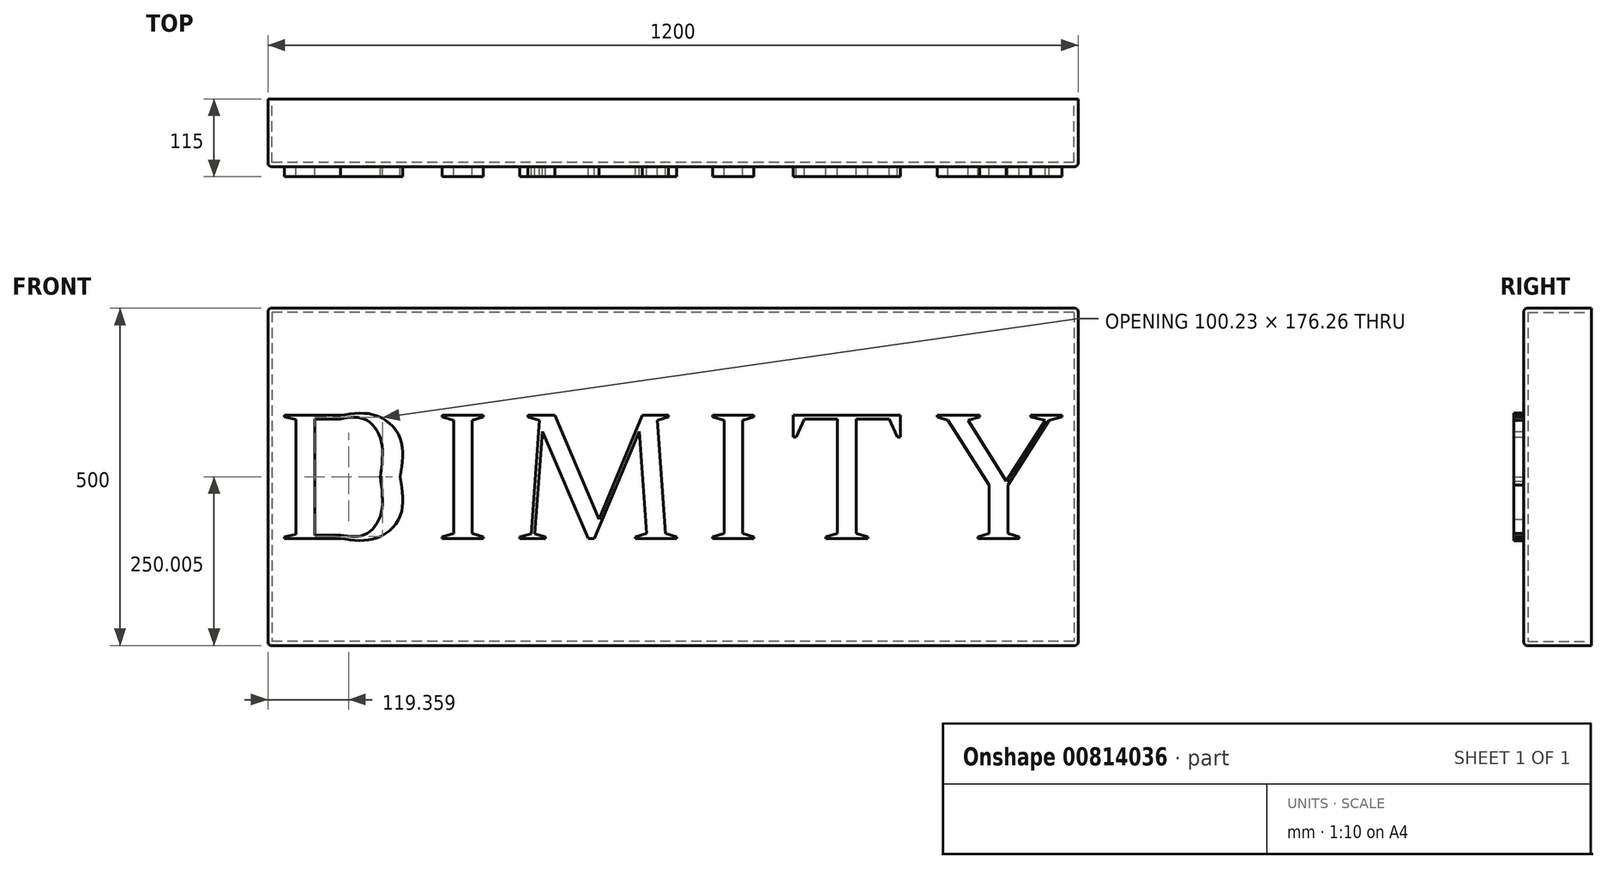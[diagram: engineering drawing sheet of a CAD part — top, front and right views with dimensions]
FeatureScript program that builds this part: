
annotation { "Feature Type Name" : "Feature", "Feature Type Description" : "" }
export const myFeature = defineFeature(function(context is Context, id is Id, definition is map)
    precondition{}
    {
        {
            var Q0;
            Q0=qCreatedBy(makeId("Front.planeOp"),FACE);
            var sketch = newSketch(context, id + "F0", { "sketchPlane" : qUnion([Q0])});
            skLineSegment(sketch, "E0", {"start": v(-575.86, 131.85) * mm, "end": v(-575.86, 129.5) * mm});
            skLineSegment(sketch, "E1", {"start": v(-575.86, 129.5) * mm, "end": v(-558.92, 125.59) * mm});
            skLineSegment(sketch, "E2", {"start": v(-558.92, 125.59) * mm, "end": v(-558.92, -44.41) * mm});
            skLineSegment(sketch, "E3", {"start": v(-558.92, -44.41) * mm, "end": v(-575.86, -48.59) * mm});
            skLineSegment(sketch, "E4", {"start": v(-575.86, -48.59) * mm, "end": v(-575.86, -50.67) * mm});
            skLineSegment(sketch, "E5", {"start": v(-575.86, -50.67) * mm, "end": v(-492.69, -50.67) * mm});
            skFitSpline(sketch, "E6", {"points": [v(-492.69, -50.67) * mm, v(-440.54, -50.67) * mm, v(-404.04, -16.78) * mm, v(-404.04, 40.59) * mm]});
            skFitSpline(sketch, "E7", {"points": [v(-404.04, 40.59) * mm, v(-404.04, 97.43) * mm, v(-440.54, 131.85) * mm, v(-492.69, 131.85) * mm]});
            skLineSegment(sketch, "E8", {"start": v(-492.69, 131.85) * mm, "end": v(-575.86, 131.85) * mm});
            skLineSegment(sketch, "E9", {"start": v(-530.76, 126.63) * mm, "end": v(-492.69, 126.63) * mm});
            skFitSpline(sketch, "E10", {"points": [v(-492.69, 126.63) * mm, v(-458.27, 126.63) * mm, v(-433.5, 97.95) * mm, v(-433.5, 40.33) * mm]});
            skFitSpline(sketch, "E11", {"points": [v(-433.5, 40.33) * mm, v(-433.5, -17.04) * mm, v(-458.27, -45.46) * mm, v(-492.69, -45.46) * mm]});
            skLineSegment(sketch, "E12", {"start": v(-492.69, -45.46) * mm, "end": v(-530.76, -45.46) * mm});
            skLineSegment(sketch, "E13", {"start": v(-530.76, -45.46) * mm, "end": v(-530.76, 126.63) * mm});
            skLineSegment(sketch, "E14", {"start": v(-341.97, 131.85) * mm, "end": v(-341.97, 129.24) * mm});
            skLineSegment(sketch, "E15", {"start": v(-341.97, 129.24) * mm, "end": v(-325.02, 124.28) * mm});
            skLineSegment(sketch, "E16", {"start": v(-325.02, 124.28) * mm, "end": v(-325.02, -43.11) * mm});
            skLineSegment(sketch, "E17", {"start": v(-325.02, -43.11) * mm, "end": v(-341.97, -48.06) * mm});
            skLineSegment(sketch, "E18", {"start": v(-341.97, -48.06) * mm, "end": v(-341.97, -50.67) * mm});
            skLineSegment(sketch, "E19", {"start": v(-341.97, -50.67) * mm, "end": v(-281.21, -50.67) * mm});
            skLineSegment(sketch, "E20", {"start": v(-281.21, -50.67) * mm, "end": v(-281.21, -48.06) * mm});
            skLineSegment(sketch, "E21", {"start": v(-281.21, -48.06) * mm, "end": v(-297.38, -43.11) * mm});
            skLineSegment(sketch, "E22", {"start": v(-297.38, -43.11) * mm, "end": v(-297.38, 124.28) * mm});
            skLineSegment(sketch, "E23", {"start": v(-297.38, 124.28) * mm, "end": v(-281.21, 129.24) * mm});
            skLineSegment(sketch, "E24", {"start": v(-281.21, 129.24) * mm, "end": v(-281.21, 131.85) * mm});
            skLineSegment(sketch, "E25", {"start": v(-281.21, 131.85) * mm, "end": v(-341.97, 131.85) * mm});
            skLineSegment(sketch, "E26", {"start": v(-214.99, 131.85) * mm, "end": v(-214.99, 129.24) * mm});
            skLineSegment(sketch, "E27", {"start": v(-214.99, 129.24) * mm, "end": v(-198.04, 124.28) * mm});
            skLineSegment(sketch, "E28", {"start": v(-198.04, 124.28) * mm, "end": v(-210.3, -43.63) * mm});
            skLineSegment(sketch, "E29", {"start": v(-210.3, -43.63) * mm, "end": v(-227.24, -48.59) * mm});
            skLineSegment(sketch, "E30", {"start": v(-227.24, -48.59) * mm, "end": v(-227.24, -50.67) * mm});
            skLineSegment(sketch, "E31", {"start": v(-227.24, -50.67) * mm, "end": v(-188.91, -50.67) * mm});
            skLineSegment(sketch, "E32", {"start": v(-188.91, -50.67) * mm, "end": v(-188.91, -48.59) * mm});
            skLineSegment(sketch, "E33", {"start": v(-188.91, -48.59) * mm, "end": v(-204.82, -43.63) * mm});
            skLineSegment(sketch, "E34", {"start": v(-204.82, -43.63) * mm, "end": v(-193.6, 108.12) * mm});
            skLineSegment(sketch, "E35", {"start": v(-193.6, 108.12) * mm, "end": v(-125.55, -50.67) * mm});
            skLineSegment(sketch, "E36", {"start": v(-125.55, -50.67) * mm, "end": v(-116.95, -50.67) * mm});
            skLineSegment(sketch, "E37", {"start": v(-116.95, -50.67) * mm, "end": v(-49.94, 107.86) * mm});
            skLineSegment(sketch, "E38", {"start": v(-49.94, 107.86) * mm, "end": v(-38.99, -43.11) * mm});
            skLineSegment(sketch, "E39", {"start": v(-38.99, -43.11) * mm, "end": v(-55.94, -48.06) * mm});
            skLineSegment(sketch, "E40", {"start": v(-55.94, -48.06) * mm, "end": v(-55.94, -50.67) * mm});
            skLineSegment(sketch, "E41", {"start": v(-55.94, -50.67) * mm, "end": v(5.08, -50.67) * mm});
            skLineSegment(sketch, "E42", {"start": v(5.08, -50.67) * mm, "end": v(5.08, -48.06) * mm});
            skLineSegment(sketch, "E43", {"start": v(5.08, -48.06) * mm, "end": v(-11.1, -43.11) * mm});
            skLineSegment(sketch, "E44", {"start": v(-11.1, -43.11) * mm, "end": v(-23.08, 124.28) * mm});
            skLineSegment(sketch, "E45", {"start": v(-23.08, 124.28) * mm, "end": v(-6.92, 129.24) * mm});
            skLineSegment(sketch, "E46", {"start": v(-6.92, 129.24) * mm, "end": v(-6.92, 131.85) * mm});
            skLineSegment(sketch, "E47", {"start": v(-6.92, 131.85) * mm, "end": v(-45.25, 131.85) * mm});
            skLineSegment(sketch, "E48", {"start": v(-45.25, 131.85) * mm, "end": v(-109.9, -21.99) * mm});
            skLineSegment(sketch, "E49", {"start": v(-109.9, -21.99) * mm, "end": v(-175.1, 131.85) * mm});
            skLineSegment(sketch, "E50", {"start": v(-175.1, 131.85) * mm, "end": v(-214.99, 131.85) * mm});
            skLineSegment(sketch, "E51", {"start": v(58.54, 131.85) * mm, "end": v(58.54, 129.24) * mm});
            skLineSegment(sketch, "E52", {"start": v(58.54, 129.24) * mm, "end": v(75.5, 124.28) * mm});
            skLineSegment(sketch, "E53", {"start": v(75.5, 124.28) * mm, "end": v(75.5, -43.11) * mm});
            skLineSegment(sketch, "E54", {"start": v(75.5, -43.11) * mm, "end": v(58.54, -48.06) * mm});
            skLineSegment(sketch, "E55", {"start": v(58.54, -48.06) * mm, "end": v(58.54, -50.67) * mm});
            skLineSegment(sketch, "E56", {"start": v(58.54, -50.67) * mm, "end": v(119.3, -50.67) * mm});
            skLineSegment(sketch, "E57", {"start": v(119.3, -50.67) * mm, "end": v(119.3, -48.06) * mm});
            skLineSegment(sketch, "E58", {"start": v(119.3, -48.06) * mm, "end": v(103.13, -43.11) * mm});
            skLineSegment(sketch, "E59", {"start": v(103.13, -43.11) * mm, "end": v(103.13, 124.28) * mm});
            skLineSegment(sketch, "E60", {"start": v(103.13, 124.28) * mm, "end": v(119.3, 129.24) * mm});
            skLineSegment(sketch, "E61", {"start": v(119.3, 129.24) * mm, "end": v(119.3, 131.85) * mm});
            skLineSegment(sketch, "E62", {"start": v(119.3, 131.85) * mm, "end": v(58.54, 131.85) * mm});
            skLineSegment(sketch, "E63", {"start": v(178.23, 131.85) * mm, "end": v(178.23, 99.77) * mm});
            skLineSegment(sketch, "E64", {"start": v(178.23, 99.77) * mm, "end": v(182.4, 99.77) * mm});
            skLineSegment(sketch, "E65", {"start": v(182.4, 99.77) * mm, "end": v(194.65, 126.63) * mm});
            skLineSegment(sketch, "E66", {"start": v(194.65, 126.63) * mm, "end": v(243.15, 126.63) * mm});
            skLineSegment(sketch, "E67", {"start": v(243.15, 126.63) * mm, "end": v(243.15, -43.11) * mm});
            skLineSegment(sketch, "E68", {"start": v(243.15, -43.11) * mm, "end": v(226.2, -48.06) * mm});
            skLineSegment(sketch, "E69", {"start": v(226.2, -48.06) * mm, "end": v(226.2, -50.67) * mm});
            skLineSegment(sketch, "E70", {"start": v(226.2, -50.67) * mm, "end": v(288.26, -50.67) * mm});
            skLineSegment(sketch, "E71", {"start": v(288.26, -50.67) * mm, "end": v(288.26, -48.06) * mm});
            skLineSegment(sketch, "E72", {"start": v(288.26, -48.06) * mm, "end": v(271.31, -43.11) * mm});
            skLineSegment(sketch, "E73", {"start": v(271.31, -43.11) * mm, "end": v(271.31, 126.63) * mm});
            skLineSegment(sketch, "E74", {"start": v(271.31, 126.63) * mm, "end": v(320.07, 126.63) * mm});
            skLineSegment(sketch, "E75", {"start": v(320.07, 126.63) * mm, "end": v(332.06, 99.77) * mm});
            skLineSegment(sketch, "E76", {"start": v(332.06, 99.77) * mm, "end": v(336.5, 99.77) * mm});
            skLineSegment(sketch, "E77", {"start": v(336.5, 99.77) * mm, "end": v(336.5, 131.85) * mm});
            skLineSegment(sketch, "E78", {"start": v(336.5, 131.85) * mm, "end": v(178.23, 131.85) * mm});
            skLineSegment(sketch, "E79", {"start": v(391.26, 131.85) * mm, "end": v(391.26, 129.24) * mm});
            skLineSegment(sketch, "E80", {"start": v(391.26, 129.24) * mm, "end": v(407.43, 124.28) * mm});
            skLineSegment(sketch, "E81", {"start": v(407.43, 124.28) * mm, "end": v(468.44, 28.6) * mm});
            skLineSegment(sketch, "E82", {"start": v(468.44, 28.6) * mm, "end": v(468.44, -43.11) * mm});
            skLineSegment(sketch, "E83", {"start": v(468.44, -43.11) * mm, "end": v(451.5, -48.06) * mm});
            skLineSegment(sketch, "E84", {"start": v(451.5, -48.06) * mm, "end": v(451.5, -50.67) * mm});
            skLineSegment(sketch, "E85", {"start": v(451.5, -50.67) * mm, "end": v(512.5, -50.67) * mm});
            skLineSegment(sketch, "E86", {"start": v(512.5, -50.67) * mm, "end": v(512.5, -48.06) * mm});
            skLineSegment(sketch, "E87", {"start": v(512.5, -48.06) * mm, "end": v(496.34, -43.11) * mm});
            skLineSegment(sketch, "E88", {"start": v(496.34, -43.11) * mm, "end": v(496.34, 28.6) * mm});
            skLineSegment(sketch, "E89", {"start": v(496.34, 28.6) * mm, "end": v(557.35, 124.28) * mm});
            skLineSegment(sketch, "E90", {"start": v(557.35, 124.28) * mm, "end": v(575.86, 129.24) * mm});
            skLineSegment(sketch, "E91", {"start": v(575.86, 129.24) * mm, "end": v(575.86, 131.85) * mm});
            skLineSegment(sketch, "E92", {"start": v(575.86, 131.85) * mm, "end": v(529.46, 131.85) * mm});
            skLineSegment(sketch, "E93", {"start": v(529.46, 131.85) * mm, "end": v(529.46, 129.24) * mm});
            skLineSegment(sketch, "E94", {"start": v(529.46, 129.24) * mm, "end": v(551.36, 124.28) * mm});
            skLineSegment(sketch, "E95", {"start": v(551.36, 124.28) * mm, "end": v(493.74, 34.33) * mm});
            skLineSegment(sketch, "E96", {"start": v(493.74, 34.33) * mm, "end": v(436.9, 124.28) * mm});
            skLineSegment(sketch, "E97", {"start": v(436.9, 124.28) * mm, "end": v(454.1, 129.24) * mm});
            skLineSegment(sketch, "E98", {"start": v(454.1, 129.24) * mm, "end": v(454.1, 131.85) * mm});
            skLineSegment(sketch, "E99", {"start": v(454.1, 131.85) * mm, "end": v(391.26, 131.85) * mm});
            skSolve(sketch);
        }
        {
            var Q0;
            Q0=qSketchRegion(id+"F0",true);
            extrude(context, id + "F1", {"entities" : qUnion([Q0]), "depth" : 15 * mm, "offsetDistance" : 25 * mm});
        }
        {
            var Q0;
            Q0=qCreatedBy(makeId("Front.planeOp"),FACE);
            var sketch = newSketch(context, id + "F2", { "sketchPlane" : qUnion([Q0])});
            skLineSegment(sketch, "E100.bottom", {"start": v(600, 290.59) * mm, "end": v(-600, 290.59) * mm});
            skLineSegment(sketch, "E100.top", {"start": v(600, -209.41) * mm, "end": v(-600, -209.41) * mm});
            skLineSegment(sketch, "E100.left", {"start": v(600, 290.59) * mm, "end": v(600, -209.41) * mm});
            skLineSegment(sketch, "E100.right", {"start": v(-600, 290.59) * mm, "end": v(-600, -209.41) * mm});
            skLineSegment(sketch, "E101", {"start": v(0, -209.41) * mm, "end": v(-600, -209.41) * mm, "construction": true});
            skLineSegment(sketch, "E102", {"start": v(-600, 265.59) * mm, "end": v(600, 265.59) * mm, "construction": true});
            skLineSegment(sketch, "E103", {"start": v(600, -184.41) * mm, "end": v(-600, -184.41) * mm, "construction": true});
            skLineSegment(sketch, "E104", {"start": v(0, 290.59) * mm, "end": v(0, -209.41) * mm, "construction": true});
            skLineSegment(sketch, "E105", {"start": v(590, 290.59) * mm, "end": v(590, -209.41) * mm, "construction": true});
            skLineSegment(sketch, "E106", {"start": v(-590, 290.59) * mm, "end": v(-590, -209.41) * mm, "construction": true});
            skLineSegment(sketch, "E107", {"start": v(678.58, 131.85) * mm, "end": v(-722.76, 131.85) * mm, "construction": true});
            skLineSegment(sketch, "E108", {"start": v(702.08, -50.67) * mm, "end": v(-703.08, -50.67) * mm, "construction": true});
            skLineSegment(sketch, "E109", {"start": v(-758.26, 40.59) * mm, "end": v(803.62, 40.59) * mm, "construction": true});
            skSolve(sketch);
        }
        {
            var Q0;
            Q0=qSketchRegion(id+"F2",true);
            extrude(context, id + "F3", {"entities" : qUnion([Q0]), "oppositeDirection" : true, "depth" : 100 * mm, "offsetDistance" : 25 * mm});
        }
        {
            var Q0;
            Q0=makeQuery(id+"F3.opExtrude","CAP_FACE",FACE,{"disambiguationData":[OSD([sQuery(id+"F2.wireOp",EDGE,"E100.bottom"),sQuery(id+"F2.wireOp",EDGE,"E100.top"),sQuery(id+"F2.wireOp",EDGE,"E100.left"),sQuery(id+"F2.wireOp",EDGE,"E100.right")])],"isStart":false});
            var sketch = newSketch(context, id + "F4", { "sketchPlane" : qUnion([Q0])});
            skSolve(sketch);
        }
        {
            var Q0;
            Q0=makeQuery(id+"F4.imprint","IMPRINT",FACE,{"disambiguationData":[TD([[makeQuery(id+"F4.imprint","IMPRINT",EDGE,{"derivedFrom":makeQuery(id+"F3.opExtrude","CAP_EDGE",EDGE,{"disambiguationData":[OSD([sQuery(id+"F2.wireOp",EDGE,"E100.bottom")])],"isStart":false})}),-1.0]])]});
            var sketch = newSketch(context, id + "F5", { "sketchPlane" : qUnion([Q0])});
            skLineSegment(sketch, "E110.bottom", {"start": v(-594, 284.59) * mm, "end": v(594, 284.59) * mm});
            skLineSegment(sketch, "E110.top", {"start": v(-594, -203.41) * mm, "end": v(594, -203.41) * mm});
            skLineSegment(sketch, "E110.left", {"start": v(-594, 284.59) * mm, "end": v(-594, -203.41) * mm});
            skLineSegment(sketch, "E110.right", {"start": v(594, 284.59) * mm, "end": v(594, -203.41) * mm});
            skSolve(sketch);
        }
        {
            var Q0;
            Q0 = qSketchRegion(id + "F5", true);
            extrude(context, id + "F6", {"entities" : qUnion([Q0]), "operationType" : NewBodyOperationType.REMOVE, "oppositeDirection" : true, "depth" : 94 * mm, "offsetDistance" : 25 * mm});
        }
        {
            var Q0;
            Q0=makeQuery(id+"F3.opExtrude","CAP_EDGE",EDGE,{"disambiguationData":[OSD([sQuery(id+"F2.wireOp",EDGE,"E100.bottom")])],"isStart":true});
            var Q1;
            Q1=makeQuery(id+"F3.opExtrude","CAP_EDGE",EDGE,{"disambiguationData":[OSD([sQuery(id+"F2.wireOp",EDGE,"E100.right")])],"isStart":true});
            var Q2;
            Q2=makeQuery(id+"F3.opExtrude","CAP_EDGE",EDGE,{"disambiguationData":[OSD([sQuery(id+"F2.wireOp",EDGE,"E100.top")])],"isStart":true});
            var Q3;
            Q3=makeQuery(id+"F3.opExtrude","CAP_EDGE",EDGE,{"disambiguationData":[OSD([sQuery(id+"F2.wireOp",EDGE,"E100.left")])],"isStart":true});
            var Q4;
            Q4=makeQuery(id+"F3.opExtrude","SWEPT_EDGE",EDGE,{"disambiguationData":[OSD([sQuery(id+"F2.wireOp",EDGE,"E100.bottom"),sQuery(id+"F2.wireOp",EDGE,"E100.left")])]});
            var Q5;
            Q5=makeQuery(id+"F3.opExtrude","SWEPT_EDGE",EDGE,{"disambiguationData":[OSD([sQuery(id+"F2.wireOp",EDGE,"E100.top"),sQuery(id+"F2.wireOp",EDGE,"E100.left")])]});
            var Q6;
            Q6=makeQuery(id+"F3.opExtrude","SWEPT_EDGE",EDGE,{"disambiguationData":[OSD([sQuery(id+"F2.wireOp",EDGE,"E100.bottom"),sQuery(id+"F2.wireOp",EDGE,"E100.right")])]});
            var Q7;
            Q7=makeQuery(id+"F3.opExtrude","SWEPT_EDGE",EDGE,{"disambiguationData":[OSD([sQuery(id+"F2.wireOp",EDGE,"E100.top"),sQuery(id+"F2.wireOp",EDGE,"E100.right")])]});
            fillet(context, id + "F7", {"entities" : qUnion([Q0, Q1, Q2, Q3, Q4, Q5, Q6, Q7]), "radius" : 5 * mm, "tangentPropagation" : true, "allowEdgeOverflow" : false});
        }
    });
